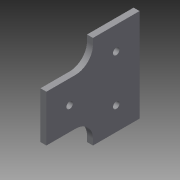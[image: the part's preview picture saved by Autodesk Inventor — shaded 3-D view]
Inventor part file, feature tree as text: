
AUTODESK INVENTOR PART (.ipt)
format: ipt  version: 2015 (Build 190159000, 159)  size: 83,968 bytes
history: native  units: in
note: dims shown in document units (in); Inventor stores cm internally (conversion verified against a paired STEP export)
features: extrude x1, sketch x1
ambient origin geometry x8: Origin, YZ Plane, XZ Plane, XY Plane, X Axis, Y Axis, Z Axis, Center Point
bodies: Solid1 (feature_tree)
feature tree (2):
  extrude  "Extrusion1"  [1 undecoded]
  sketch  "Sketch1"  dims[d0=0.128in d1=0.0in]
note: 1 required parameter value undecoded (feature->parameter linkage not recoverable at this tier; creation-order binding heuristic only, values carry confidence <= 0.55)
